# Revit family: Oval kiinteä tukikaide
name_source: partatom
category: Specialty Equipment
revit_build: Autodesk Revit 2015 (Build: 20160512_0715(x64)
units: mm (PartAtom-declared; Revit-internal decimal feet)

## types (4) — shared parameters
Assembly Code = 1336
Frame Colour = RAL 9016 - White
Height = 204 mm
Keynote = 523
Manufacturer = Väinö Korpinen Oy
Model = Oval
Support Height = 800 mm  [stored 2.62467 ft]
Thickness = 30 mm  [stored 0.0984252 ft]
URL = https://korpinen.com
Width = 125 mm  [stored 0.410105 ft]

## per-type parameters (varying)
| type | 720 | 820 | Colour | Depth | Model ID |
| 20111G harmaa | Yes | No | Elastomer - Grey | 720 mm  [stored 2.3622 ft] | 20111G |
| 20115G harmaa | No | Yes | Elastomer - Grey | 820 mm  [stored 2.69029 ft] | 20115G |
| 20111R punainen | Yes | No | Elastomer - Red | 720 mm  [stored 2.3622 ft] | 20111R |
| 20115R punainen | No | Yes | Elastomer - Red | 820 mm  [stored 2.69029 ft] | 20115R |

note: [stored X ft] marks values corroborated as IEEE doubles in the binary element streams (Revit-internal decimal feet)

## geometry (parser evidence)
native form markers: Blend x6, Sweep x13
no freeform markers — native parametric forms only
